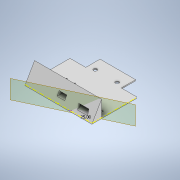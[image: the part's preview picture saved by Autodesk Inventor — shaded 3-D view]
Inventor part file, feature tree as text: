
AUTODESK INVENTOR PART (.ipt)
format: ipt  version: 2021 (Build 250183000, 183)  size: 288,768 bytes
history: native  units: mm
features: sketch x11, extrude x10, other x1, plane x1
ambient origin geometry x8: Origin, YZ Plane, XZ Plane, XY Plane, X Axis, Y Axis, Z Axis, Center Point
bodies: Body1 (feature_tree)
feature tree (23):
  other  "Sólido1"
  extrude  "Base"  Depth=1.5mm TaperAngle=0.0deg
  extrude  "Angulo Base"  Depth=98.0mm TaperAngle=0.0deg
  extrude  "Extrusión3"  Depth=98.0mm TaperAngle=0.0deg
  extrude  "Extrusión4"  Depth=0.9mm
  extrude  "Extrusión5"  Depth=3.9mm
  extrude  "Extrusión6"  Depth=5.6mm
  extrude  "Extrusión7"  Depth=42.5mm
  extrude  "Extrusión8"  Depth=76.25mm TaperAngle=0.0deg
  extrude  "Extrusión9"  Depth=13.0mm
  sketch  "Boceto12"  dims[d54=4.5mm d55=20.0mm d56=0.0mm]
  plane  "Plano de trabajo1"
  extrude  "Extrusión10"  Depth=20.0mm TaperAngle=0.0deg
  sketch  "Boceto1"  dims[d0=3.5mm d1=0.0mm d2=87.0mm d3=21.0mm d4=12.0mm d5=23.0mm d6=98.0mm d7=7.5mm d8=7.5mm d9=79.5mm d10=2.1mm d11=9.0mm d12=11.0mm d13=16.0mm d14=1.0mm d15=3.6mm d16=2.1mm d17=1.3mm d18=5.0mm d19=36.0mm d20=9.5mm d21=5.0mm d22=17.0mm d23=10.0mm d24=8.7mm d25=4.3mm d26=4.0mm d27=11.0mm d28=54.0mm d29=2.85mm d30=1.5mm d31=0.0mm]
  sketch  "Boceto2"  dims[d32=20.935224mm d33=98.0mm d34=0.0mm]
  sketch  "Boceto3"  dims[d35=0.0mm d36=98.0mm d37=0.0mm]
  sketch  "Boceto4"  dims[d38=13.0mm d39=0.9mm]
  sketch  "Boceto5"  dims[d40=0.9mm d41=3.9mm]
  sketch  "Boceto6"  dims[d42=5.6mm d43=18.7mm]
  sketch  "Boceto7"  dims[d44=42.5mm d45=42.5mm]
  sketch  "Boceto8"  dims[d46=3.5mm d47=76.25mm d48=0.0mm]
  sketch  "Boceto9"  dims[d49=11.2mm d50=14.8mm d51=1.5mm d52=0.0mm d53=13.0mm]
  sketch  "Boceto13"  dims[d57=4.84mm d58=6.076mm d59=11.2mm d60=0.9mm d61=4.978mm d62=11.2mm d63=0.9mm d64=0.0mm d65=5.25mm d66=0.0mm d67=3.8mm d68=11.2mm d69=10.054mm d70=0.0mm d76=4.84mm d77=1.0mm d78=3.9mm d79=0.0mm d82=4.363323mm d83=90.0deg d84=18.7mm d85=11.2mm d86=6.076mm d87=0.0mm d88=3.9mm d89=45.15mm d90=0.0mm d91=15.0mm d92=0.94mm d93=0.93988mm d71=0.5mm d72=0.872665mm d73=0.5mm d74=0.872665mm]
